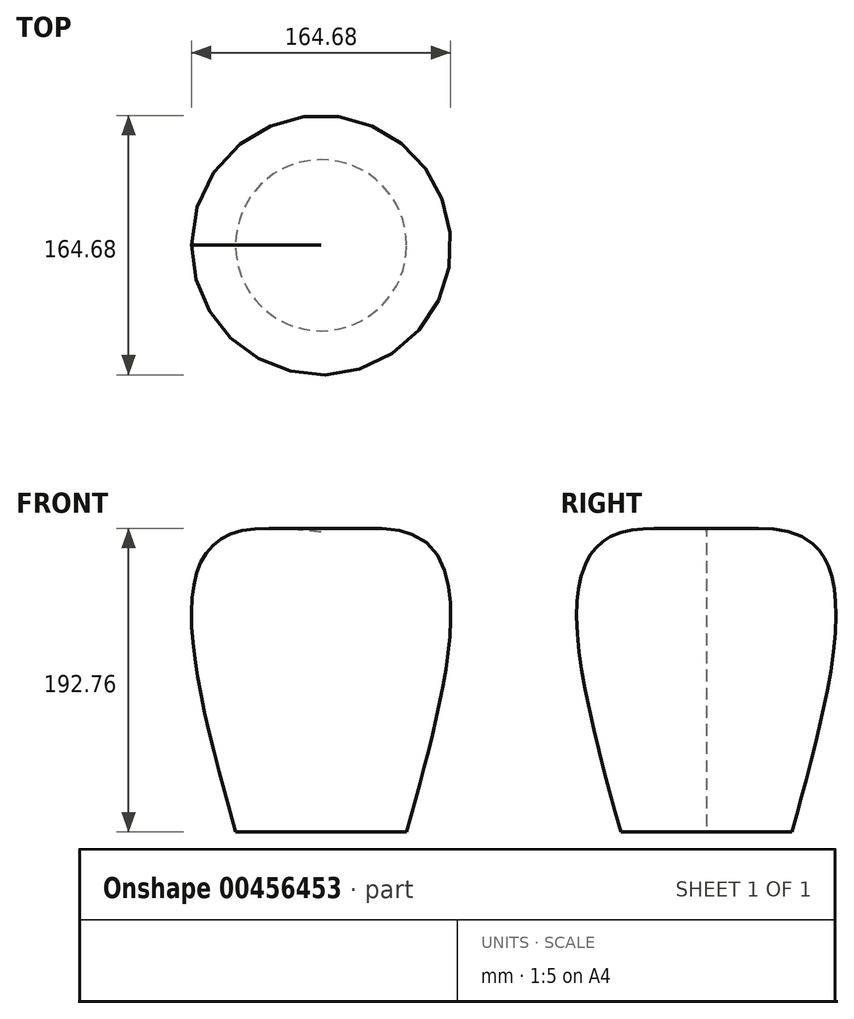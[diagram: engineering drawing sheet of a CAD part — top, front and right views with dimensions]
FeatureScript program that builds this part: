
annotation { "Feature Type Name" : "Feature", "Feature Type Description" : "" }
export const myFeature = defineFeature(function(context is Context, id is Id, definition is map)
    precondition{}
    {
        {
            var Q0;
            Q0=qCreatedBy(makeId("Top.planeOp"),FACE);
            var sketch = newSketch(context, id + "F0", { "sketchPlane" : qUnion([Q0])});
            skCircle(sketch, "E0", {"center": v(0, 0) * mm, "radius": 54.34 * mm});
            skSolve(sketch);
        }
        {
            var Q0;
            Q0=makeQuery(id+"F0.imprint","IMPRINT",FACE,{"disambiguationData":[TD([[makeQuery(id+"F0.imprint","IMPRINT",EDGE,{"derivedFrom":sQuery(id+"F0.wireOp",EDGE,"E0")}),1.0]])]});
            cPlane(context, id + "F1", {"entities" : qUnion([Q0]), "cplaneType" : CPlaneType.OFFSET, "offset" : 190.5 * mm, "width" : 152.4 * mm, "height" : 152.4 * mm});
        }
        {
            var Q0;
            Q0=qCreatedBy(id+"F1.planeOp",FACE);
            var sketch = newSketch(context, id + "F2", { "sketchPlane" : qUnion([Q0])});
            skCircle(sketch, "E1", {"center": v(0, 0) * mm, "radius": 53.48 * mm});
            skSolve(sketch);
        }
        {
            var Q0;
            Q0=sQuery(id+"F2.wireOp",VERTEX,"E1.center");
            var Q1;
            Q1=makeQuery(id+"F2.imprint","IMPRINT",FACE,{"disambiguationData":[TD([[makeQuery(id+"F2.imprint","IMPRINT",EDGE,{"derivedFrom":sQuery(id+"F2.wireOp",EDGE,"E1")}),1.0]])]});
            var Q2;
            Q2=sQuery(id+"F0.wireOp",EDGE,"E0");
            loft(context, id + "F3", {"bodyType" : ToolBodyType.SURFACE, "wireProfilesArray" : [{ "wireProfileEntities" : qUnion([Q0]) }, { "wireProfileEntities" : qUnion([Q1]) }, { "wireProfileEntities" : qUnion([Q2]) }]});
        }
    });
